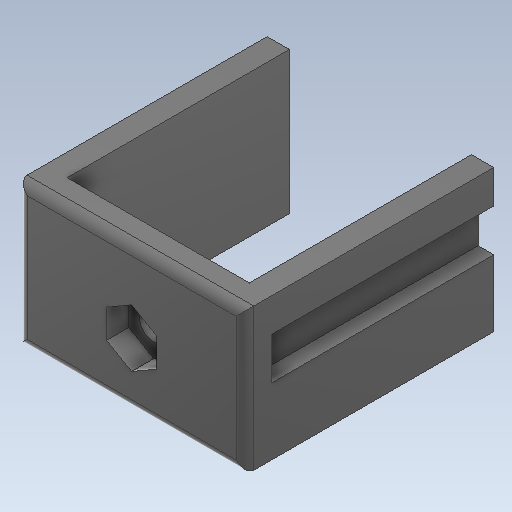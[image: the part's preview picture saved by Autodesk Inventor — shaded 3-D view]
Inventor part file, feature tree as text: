
AUTODESK INVENTOR PART (.ipt)
format: ipt  version: 2020 (Build 240168000, 168)  size: 483,328 bytes
history: native  units: mm
features: extrude x6, projected_geometry x6, sketch x4, fillet x2
ambient origin geometry x8: Origin, YZ Plane, XZ Plane, XY Plane, X Axis, Y Axis, Z Axis, Center Point
bodies: Body1 (feature_tree)
feature tree (18):
  extrude  "Выдавливание7"  Depth=4.0mm
  extrude  "Выдавливание16"  Depth=25.5mm
  sketch  "Эскиз12"
  extrude  "Выдавливание17"  Depth=3.0mm
  extrude  "Выдавливание18"  Depth=3.0mm
  extrude  "Выдавливание19"  Depth=3.0mm
  fillet  "Сопряжение1"  Radius=20.2mm
  extrude  "Выдавливание20"  Depth=14.0mm TaperAngle=0.0deg
  fillet  "Сопряжение2"  Radius=26.0mm
  sketch  "Эскиз1"
  sketch  "Эскиз10"
  projected_geometry  "Спроецированная петля9"
  projected_geometry  "Спроецированная петля10"
  projected_geometry  "Спроецированная петля11"
  projected_geometry  "Спроецированная петля12"
  projected_geometry  "Спроецированная петля13"
  sketch  "Эскиз14"
  projected_geometry  "Спроецированная петля15"
